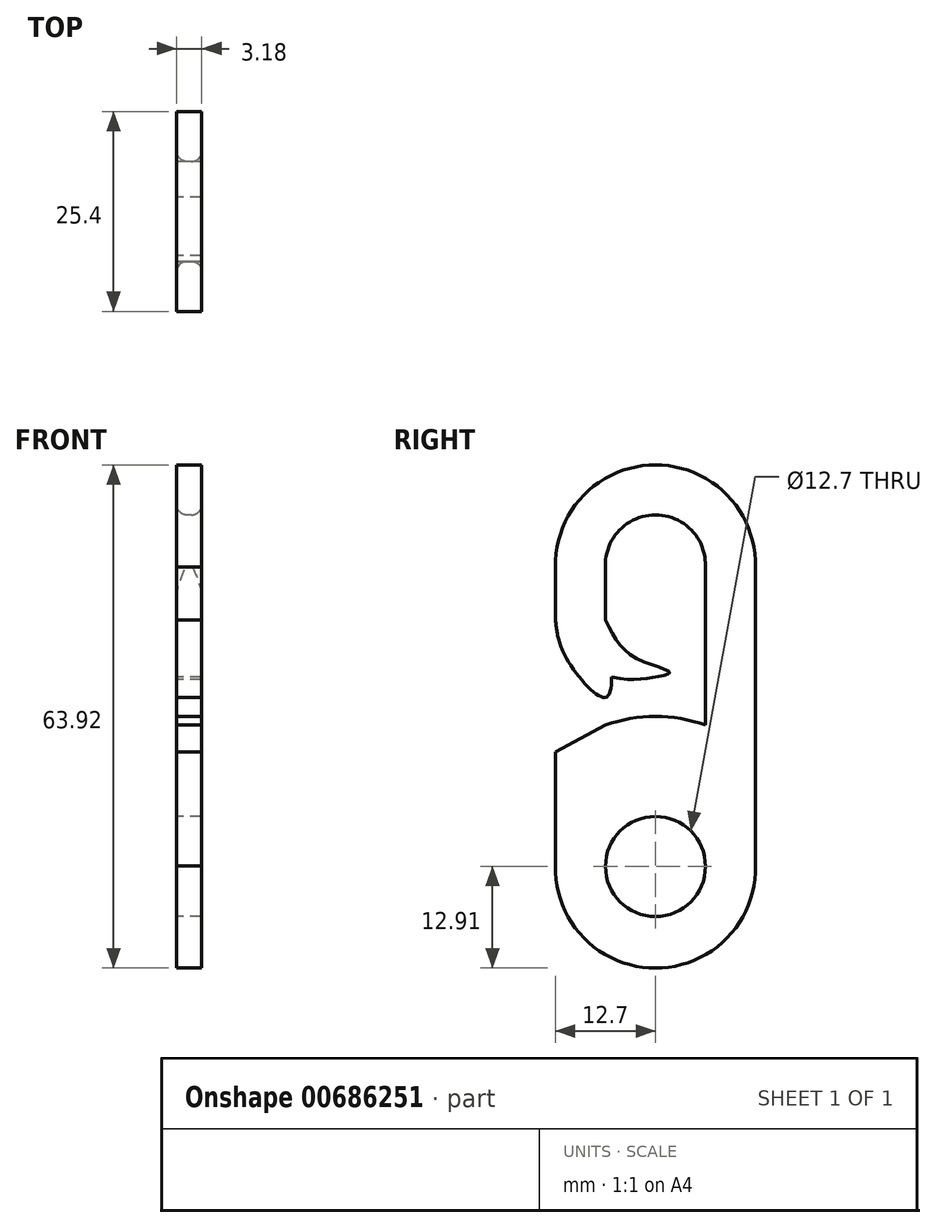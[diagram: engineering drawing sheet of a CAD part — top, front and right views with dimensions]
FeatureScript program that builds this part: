
annotation { "Feature Type Name" : "Feature", "Feature Type Description" : "" }
export const myFeature = defineFeature(function(context is Context, id is Id, definition is map)
    precondition{}
    {
        {
            var Q0;
            Q0=qCreatedBy(makeId("Right.planeOp"),FACE);
            var sketch = newSketch(context, id + "F0", { "sketchPlane" : qUnion([Q0])});
            skLineSegment(sketch, "E0.left", {"start": v(6.35, -1.09) * mm, "end": v(6.35, 19.05) * mm});
            skPoint(sketch, "E0.middle", {"position": v(0, 0) * mm});
            skArc(sketch, "E1", {"start": v(6.35, 19.05) * mm, "mid": v(0, 25.61) * mm, "end": v(-6.35, 19.05) * mm});
            skPoint(sketch, "E1.third.point", {"position": v(0, 25.61) * mm});
            skPoint(sketch, "E1.third.point.positionSnap0", {"position": v(0, 19.05) * mm});
            skPoint(sketch, "E2.MirrorP", {"position": v(0, -19.05) * mm});
            skPoint(sketch, "E3.MirrorP", {"position": v(0, -25.61) * mm});
            skPoint(sketch, "E4.MirrorCS.start.orphan", {"position": v(6.35, -19.05) * mm});
            skArc(sketch, "E5.0", {"start": v(12.7, 18.96) * mm, "mid": v(0, 31.96) * mm, "end": v(-12.7, 18.96) * mm});
            skLineSegment(sketch, "E5.1", {"start": v(12.7, -18.96) * mm, "end": v(12.7, 18.96) * mm});
            skArc(sketch, "E5.2", {"start": v(12.7, -18.96) * mm, "mid": v(0, -31.96) * mm, "end": v(-12.7, -18.96) * mm});
            skLineSegment(sketch, "E5.3", {"start": v(-12.7, -18.96) * mm, "end": v(-12.7, -4.5) * mm});
            skArc(sketch, "E6.0", {"start": v(6.35, -1.09) * mm, "mid": v(0, 0) * mm, "end": v(-6.35, -1.09) * mm});
            skPoint(sketch, "E7.MirrorC.end.orphan", {"position": v(-6.35, -19.05) * mm});
            skCircle(sketch, "E8", {"center": v(0, -19.05) * mm, "radius": 6.35 * mm});
            skLineSegment(sketch, "E9.trimOffspring", {"start": v(-12.7, 12.27) * mm, "end": v(-12.7, 18.96) * mm});
            skLineSegment(sketch, "E10.trimOffspring", {"start": v(-6.35, 12.27) * mm, "end": v(-6.35, 19.05) * mm});
            skFitSpline(sketch, "E11", {"points": [v(-12.7, 12.27) * mm, v(-11.31, 7.4) * mm, v(-6.35, 2.44) * mm, v(-6.35, 12.27) * mm], "startDerivative": vector(1.65, -15.7) * mm, "endDerivative": vector(-5.13, 36.61) * mm});
            skFitSpline(sketch, "E12", {"points": [v(-5.58, 5) * mm, v(0, 5) * mm, v(1.8, 5.6) * mm, v(-2.62, 7.5) * mm, v(-6.35, 12.27) * mm], "startDerivative": vector(25.1, -5.23) * mm, "endDerivative": vector(-10.61, 21.16) * mm});
            skFitSpline(sketch, "E13", {"points": [v(-6.35, -1.09) * mm, v(-12.7, -4.5) * mm], "startDerivative": vector(-6.35, -3.41) * mm, "endDerivative": vector(-6.35, -3.41) * mm});
            skPoint(sketch, "E14.start.orphan", {"position": v(-6.35, 5.97) * mm});
            skFitSpline(sketch, "E15", {"points": [v(-5.58, 5) * mm, v(-11.31, 7.4) * mm], "startDerivative": vector(-5.73, 2.4) * mm, "endDerivative": vector(-5.73, 2.4) * mm});
            skSolve(sketch);
        }
        {
            var Q0;
            Q0 = qSketchRegion(id + "F0", true);
            extrude(context, id + "F1", {"entities" : qUnion([Q0]), "depth" : 3.17 * mm, "offsetDistance" : 25.4 * mm});
        }
        {
            var Q0;
            Q0=makeQuery(id+"F1.opExtrude","SWEPT_FACE",FACE,{"disambiguationData":[OSD([sQuery(id+"F0.wireOp",EDGE,"E1")])]});
            var Q1;
            Q1=makeQuery(id+"F1.opExtrude","CAP_EDGE",EDGE,{"disambiguationData":[OSD([sQuery(id+"F0.wireOp",EDGE,"E1")])],"isStart":false});
            fillet(context, id + "F2", {"entities" : qUnion([Q0, Q1]), "radius" : 1.27 * mm, "tangentPropagation" : true, "allowEdgeOverflow" : false});
        }
    });
